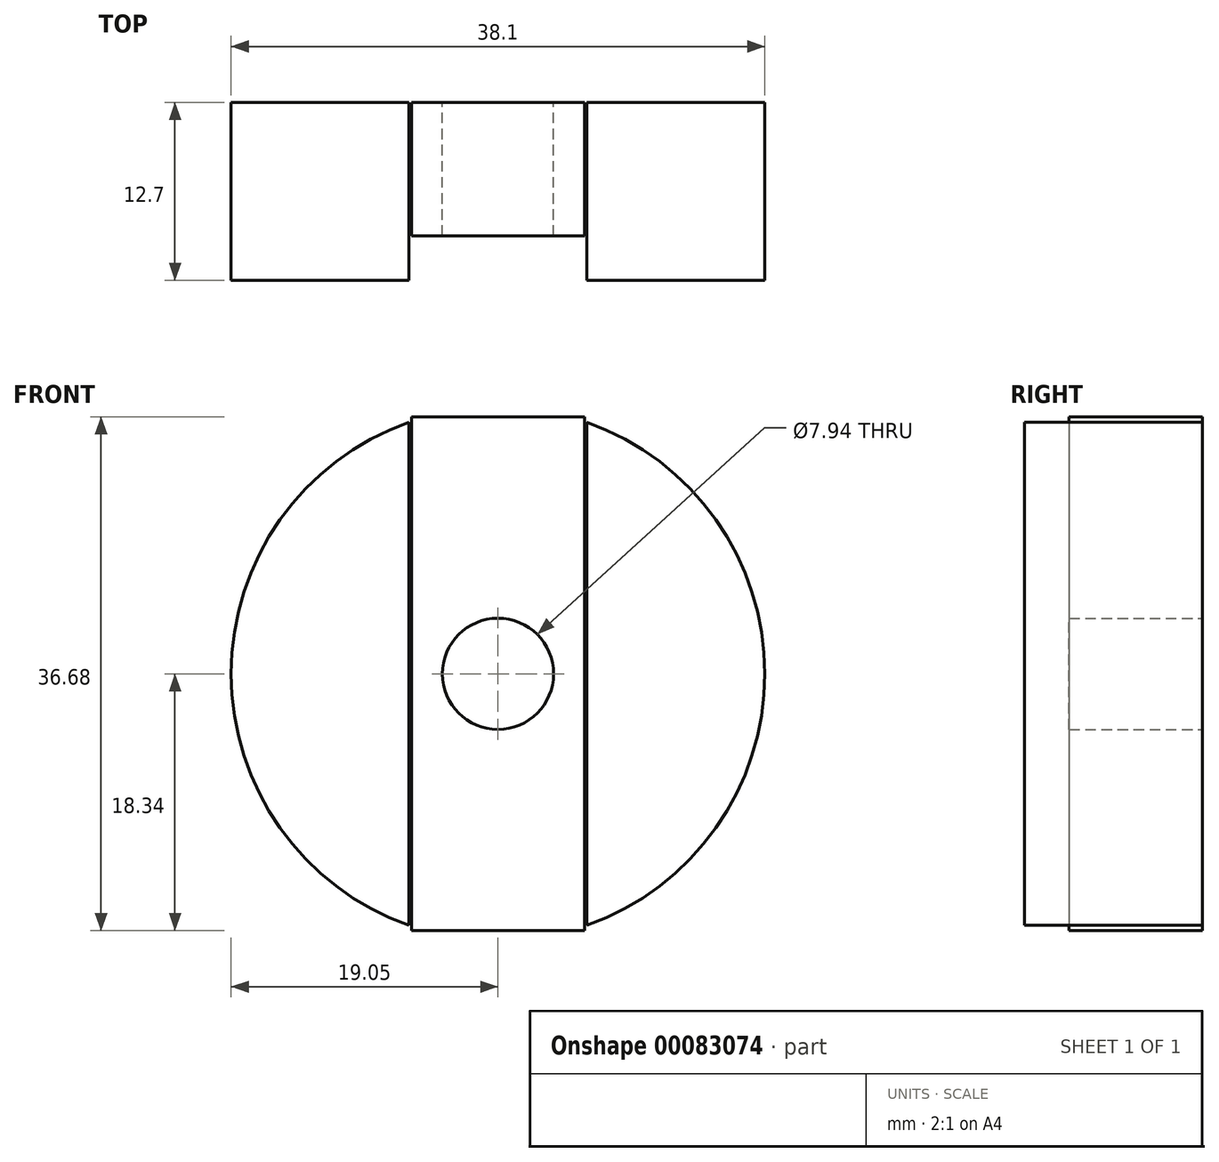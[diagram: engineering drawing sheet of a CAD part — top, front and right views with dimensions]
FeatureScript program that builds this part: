
annotation { "Feature Type Name" : "Feature", "Feature Type Description" : "" }
export const myFeature = defineFeature(function(context is Context, id is Id, definition is map)
    precondition{}
    {
        {
            var Q0;
            Q0=qCreatedBy(makeId("Front.planeOp"),FACE);
            var sketch = newSketch(context, id + "F0", { "sketchPlane" : qUnion([Q0])});
            skCircle(sketch, "E0", {"center": v(0, 0) * mm, "radius": 19.05 * mm});
            skLineSegment(sketch, "E1.bottom", {"start": v(-6.35, -17.96) * mm, "end": v(6.35, -17.96) * mm});
            skLineSegment(sketch, "E1.top", {"start": v(-6.35, 17.96) * mm, "end": v(6.35, 17.96) * mm});
            skLineSegment(sketch, "E1.left", {"start": v(-6.35, -17.96) * mm, "end": v(-6.35, 17.96) * mm});
            skLineSegment(sketch, "E1.right", {"start": v(6.35, -17.96) * mm, "end": v(6.35, 17.96) * mm});
            skCircle(sketch, "E2", {"center": v(0, 0) * mm, "radius": 3.97 * mm});
            skSolve(sketch);
        }
        {
            var Q0;
            {var subQ0=sQuery(id+"F0.wireOp",EDGE,"E1.right");Q0=makeQuery(id+"F0.imprint","IMPRINT",FACE,{"disambiguationData":[TD([[makeQuery(id+"F0.imprint","IMPRINT",EDGE,{"derivedFrom":subQ0}),-1.0]])]});}
            var Q1;
            {var subQ0=sQuery(id+"F0.wireOp",EDGE,"E1.left");Q1=makeQuery(id+"F0.imprint","IMPRINT",FACE,{"disambiguationData":[TD([[makeQuery(id+"F0.imprint","IMPRINT",EDGE,{"derivedFrom":subQ0}),1.0]])]});}
            extrude(context, id + "F1", {"entities" : qUnion([Q0, Q1]), "depth" : 12.7 * mm});
        }
        {
            var Q0;
            Q0=qCreatedBy(makeId("Front.planeOp"),FACE);
            var sketch = newSketch(context, id + "F2", { "sketchPlane" : qUnion([Q0])});
            skLineSegment(sketch, "E3.bottom", {"start": v(-6.17, 18.34) * mm, "end": v(6.17, 18.34) * mm});
            skLineSegment(sketch, "E3.top", {"start": v(-6.17, -18.34) * mm, "end": v(6.17, -18.34) * mm});
            skLineSegment(sketch, "E3.left", {"start": v(-6.17, 18.34) * mm, "end": v(-6.17, -18.34) * mm});
            skLineSegment(sketch, "E3.right", {"start": v(6.17, 18.34) * mm, "end": v(6.17, -18.34) * mm});
            skPoint(sketch, "E3.middle", {"position": v(0, 0) * mm});
            skSolve(sketch);
        }
        {
            var Q0;
            Q0=qCreatedBy(makeId("Front.planeOp"),FACE);
            var sketch = newSketch(context, id + "F3", { "sketchPlane" : qUnion([Q0])});
            skLineSegment(sketch, "E4.bottom", {"start": v(-6.35, 18.88) * mm, "end": v(6.35, 18.88) * mm});
            skLineSegment(sketch, "E4.top", {"start": v(-6.35, -18.88) * mm, "end": v(6.35, -18.88) * mm});
            skLineSegment(sketch, "E4.left", {"start": v(-6.35, 18.88) * mm, "end": v(-6.35, -18.88) * mm});
            skLineSegment(sketch, "E4.right", {"start": v(6.35, 18.88) * mm, "end": v(6.35, -18.88) * mm});
            skPoint(sketch, "E4.middle", {"position": v(0, 0) * mm});
            skSolve(sketch);
        }
        {
            var Q0;
            Q0=makeQuery(id+"F2.imprint","IMPRINT",FACE,{"disambiguationData":[TD([[makeQuery(id+"F2.imprint","IMPRINT",EDGE,{"derivedFrom":sQuery(id+"F2.wireOp",EDGE,"E3.bottom")}),-1.0]])]});
            extrude(context, id + "F4", {"entities" : qUnion([Q0]), "operationType" : NewBodyOperationType.ADD, "depth" : 9.52 * mm});
        }
        {
            var Q0;
            Q0=sQuery(id+"F3.wireOp",VERTEX,"E4.middle");
            var Q1;
            Q1=makeQuery(id+"F4.opExtrude","SWEPT_BODY",BODY,{"disambiguationData":[OSD([sQuery(id+"F2.wireOp",EDGE,"E3.bottom"),sQuery(id+"F2.wireOp",EDGE,"E3.top"),sQuery(id+"F2.wireOp",EDGE,"E3.left"),sQuery(id+"F2.wireOp",EDGE,"E3.right")])]});
            hole(context, id + "F5", {"style" : HoleStyle.SIMPLE, "endStyle" : HoleEndStyle.THROUGH, "oppositeDirection" : true, "holeDiameter" : 7.94 * mm, "locations" : qUnion([Q0]), "scope" : qUnion([Q1]), "isTappedThrough" : true});
        }
    });
